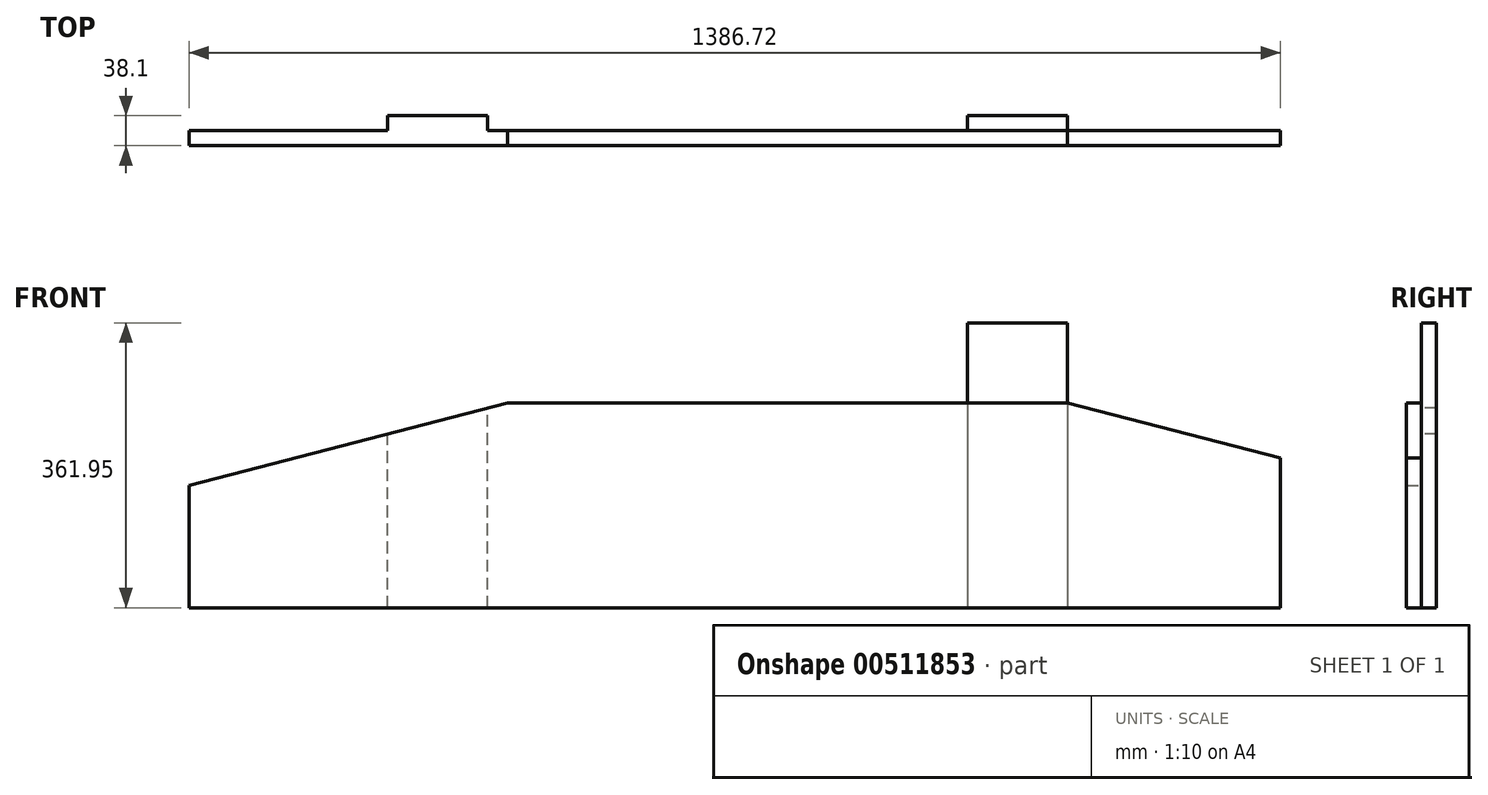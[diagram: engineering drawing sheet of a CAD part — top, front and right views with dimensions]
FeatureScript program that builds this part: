
annotation { "Feature Type Name" : "Feature", "Feature Type Description" : "" }
export const myFeature = defineFeature(function(context is Context, id is Id, definition is map)
    precondition{}
    {
        {
            var Q0;
            Q0=qCreatedBy(makeId("Front.planeOp"),FACE);
            var sketch = newSketch(context, id + "F0", { "sketchPlane" : qUnion([Q0])});
            skLineSegment(sketch, "E0", {"start": v(-678.36, -186.3) * mm, "end": v(708.36, -186.3) * mm});
            skLineSegment(sketch, "E1", {"start": v(708.36, -186.3) * mm, "end": v(708.36, 4.2) * mm});
            skLineSegment(sketch, "E2", {"start": v(708.36, 4.2) * mm, "end": v(437.83, 74.05) * mm});
            skLineSegment(sketch, "E3", {"start": v(437.83, 74.05) * mm, "end": v(-273.37, 74.05) * mm});
            skLineSegment(sketch, "E4", {"start": v(-273.37, 74.05) * mm, "end": v(-678.36, -30.72) * mm});
            skLineSegment(sketch, "E5", {"start": v(-678.36, -30.72) * mm, "end": v(-678.36, -186.3) * mm});
            skSolve(sketch);
        }
        {
            var Q0;
            Q0=makeQuery(id+"F0.imprint","IMPRINT",FACE,{"disambiguationData":[TD([[makeQuery(id+"F0.imprint","IMPRINT",EDGE,{"derivedFrom":sQuery(id+"F0.wireOp",EDGE,"E0")}),1.0]])]});
            var sketch = newSketch(context, id + "F1", { "sketchPlane" : qUnion([Q0])});
            skLineSegment(sketch, "E6", {"start": v(-298.85, -186.3) * mm, "end": v(-298.85, 194.7) * mm});
            skLineSegment(sketch, "E7", {"start": v(-298.85, -186.3) * mm, "end": v(-425.85, -186.3) * mm});
            skLineSegment(sketch, "E8", {"start": v(-425.85, -186.3) * mm, "end": v(-425.85, 93.1) * mm});
            skArc(sketch, "E9", {"start": v(-425.85, 93.1) * mm, "mid": v(-386.77, 174.42) * mm, "end": v(-298.85, 194.7) * mm});
            skCircle(sketch, "E10", {"center": v(-362.35, 143.9) * mm, "radius": 12.7 * mm});
            skSolve(sketch);
        }
        {
            var Q0;
            Q0=makeQuery(id+"F0.imprint","IMPRINT",FACE,{"disambiguationData":[TD([[makeQuery(id+"F0.imprint","IMPRINT",EDGE,{"derivedFrom":sQuery(id+"F0.wireOp",EDGE,"E0")}),1.0]])]});
            var sketch = newSketch(context, id + "F2", { "sketchPlane" : qUnion([Q0])});
            skLineSegment(sketch, "E11.bottom", {"start": v(437.83, 175.65) * mm, "end": v(310.83, 175.65) * mm});
            skLineSegment(sketch, "E11.top", {"start": v(437.83, -186.3) * mm, "end": v(310.83, -186.3) * mm});
            skLineSegment(sketch, "E11.left", {"start": v(437.83, 175.65) * mm, "end": v(437.83, -186.3) * mm});
            skLineSegment(sketch, "E11.right", {"start": v(310.83, 175.65) * mm, "end": v(310.83, -186.3) * mm});
            skSolve(sketch);
        }
        {
            var Q0;
            Q0=makeQuery(id+"F0.imprint","IMPRINT",FACE,{"disambiguationData":[TD([[makeQuery(id+"F0.imprint","IMPRINT",EDGE,{"derivedFrom":sQuery(id+"F0.wireOp",EDGE,"E0")}),1.0]])]});
            extrude(context, id + "F3", {"entities" : qUnion([Q0]), "depth" : 19.05 * mm});
        }
        {
            var Q0;
            {var subQ0=sQuery(id+"F1.wireOp",EDGE,"E9");Q0=makeQuery(id+"F1.imprint","IMPRINT",FACE,{"disambiguationData":[TD([[makeQuery(id+"F1.imprint","IMPRINT",EDGE,{"derivedFrom":subQ0}),-1.0]])]});}
            var Q1;
            {var subQ0=sQuery(id+"F1.wireOp",EDGE,"E7");Q1=makeQuery(id+"F1.imprint","IMPRINT",FACE,{"disambiguationData":[TD([[makeQuery(id+"F1.imprint","IMPRINT",EDGE,{"derivedFrom":subQ0}),1.0]])]});}
            extrude(context, id + "F4", {"entities" : qUnion([Q0, Q1]), "operationType" : NewBodyOperationType.ADD, "oppositeDirection" : true, "depth" : 19.05 * mm});
        }
        {
            var Q0;
            {var subQ0=sQuery(id+"F2.wireOp",EDGE,"E11.bottom");Q0=makeQuery(id+"F2.imprint","IMPRINT",FACE,{"disambiguationData":[TD([[makeQuery(id+"F2.imprint","IMPRINT",EDGE,{"derivedFrom":subQ0}),1.0]])]});}
            var Q1;
            {var subQ0=sQuery(id+"F2.wireOp",EDGE,"E11.top");Q1=makeQuery(id+"F2.imprint","IMPRINT",FACE,{"disambiguationData":[TD([[makeQuery(id+"F2.imprint","IMPRINT",EDGE,{"derivedFrom":subQ0}),1.0]])]});}
            extrude(context, id + "F5", {"entities" : qUnion([Q0, Q1]), "operationType" : NewBodyOperationType.ADD, "oppositeDirection" : true, "depth" : 19.05 * mm});
        }
    });
